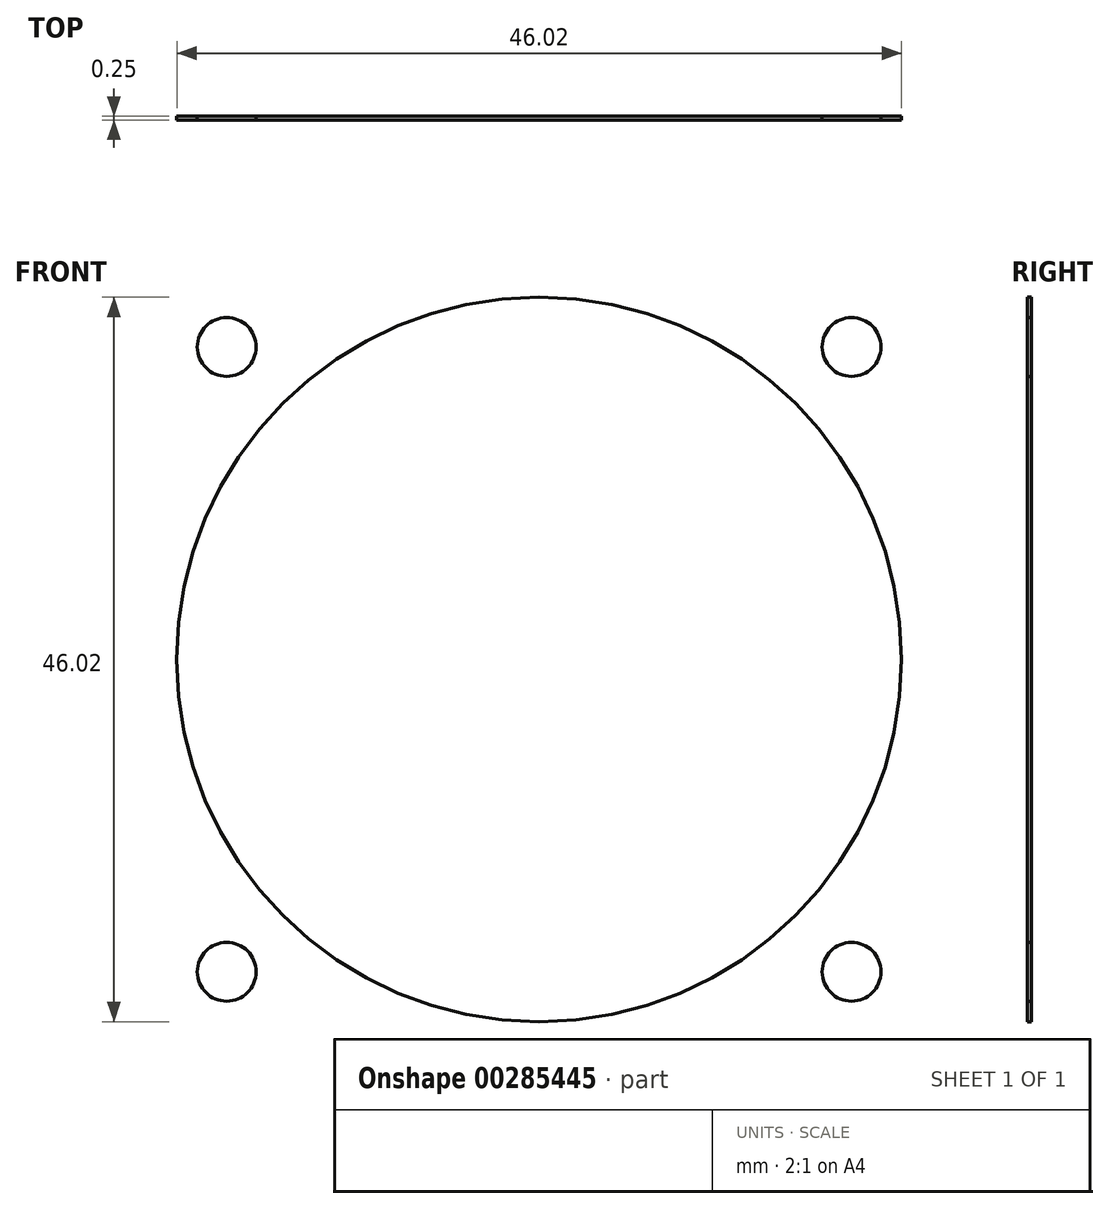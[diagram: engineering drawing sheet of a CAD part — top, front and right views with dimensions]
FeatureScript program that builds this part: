
annotation { "Feature Type Name" : "Feature", "Feature Type Description" : "" }
export const myFeature = defineFeature(function(context is Context, id is Id, definition is map)
    precondition{}
    {
        {
            var Q0;
            Q0=qCreatedBy(makeId("Front.planeOp"),FACE);
            var sketch = newSketch(context, id + "F0", { "sketchPlane" : qUnion([Q0])});
            skCircle(sketch, "E0", {"center": v(0, 0) * mm, "radius": 23.01 * mm});
            skCircle(sketch, "E1", {"center": v(-19.84, 19.84) * mm, "radius": 1.87 * mm});
            skLineSegment(sketch, "E2.bottom", {"start": v(-19.84, 19.84) * mm, "end": v(19.84, 19.84) * mm, "construction": true});
            skLineSegment(sketch, "E2.top", {"start": v(-19.84, -19.84) * mm, "end": v(19.84, -19.84) * mm, "construction": true});
            skLineSegment(sketch, "E2.left", {"start": v(-19.84, 19.84) * mm, "end": v(-19.84, -19.84) * mm, "construction": true});
            skLineSegment(sketch, "E2.right", {"start": v(19.84, 19.84) * mm, "end": v(19.84, -19.84) * mm, "construction": true});
            skLineSegment(sketch, "E3", {"start": v(0, 19.84) * mm, "end": v(0, -19.84) * mm, "construction": true});
            skLineSegment(sketch, "E4", {"start": v(-19.84, 0) * mm, "end": v(19.84, 0) * mm, "construction": true});
            skCircle(sketch, "E5", {"center": v(19.84, 19.84) * mm, "radius": 1.87 * mm});
            skCircle(sketch, "E6", {"center": v(19.84, -19.84) * mm, "radius": 1.87 * mm});
            skCircle(sketch, "E7", {"center": v(-19.84, -19.84) * mm, "radius": 1.87 * mm});
            skSolve(sketch);
        }
        {
            var Q0;
            Q0=makeQuery(id+"F0.imprint","IMPRINT",FACE,{"disambiguationData":[TD([[makeQuery(id+"F0.imprint","IMPRINT",EDGE,{"derivedFrom":sQuery(id+"F0.wireOp",EDGE,"E0")}),1.0]])]});
            var Q1;
            Q1=makeQuery(id+"F0.imprint","IMPRINT",FACE,{"disambiguationData":[TD([[makeQuery(id+"F0.imprint","IMPRINT",EDGE,{"derivedFrom":sQuery(id+"F0.wireOp",EDGE,"E1")}),1.0]])]});
            var Q2;
            Q2=makeQuery(id+"F0.imprint","IMPRINT",FACE,{"disambiguationData":[TD([[makeQuery(id+"F0.imprint","IMPRINT",EDGE,{"derivedFrom":sQuery(id+"F0.wireOp",EDGE,"E5")}),1.0]])]});
            var Q3;
            Q3=makeQuery(id+"F0.imprint","IMPRINT",FACE,{"disambiguationData":[TD([[makeQuery(id+"F0.imprint","IMPRINT",EDGE,{"derivedFrom":sQuery(id+"F0.wireOp",EDGE,"E6")}),1.0]])]});
            var Q4;
            Q4=makeQuery(id+"F0.imprint","IMPRINT",FACE,{"disambiguationData":[TD([[makeQuery(id+"F0.imprint","IMPRINT",EDGE,{"derivedFrom":sQuery(id+"F0.wireOp",EDGE,"E7")}),1.0]])]});
            extrude(context, id + "F1", {"entities" : qUnion([Q0, Q1, Q2, Q3, Q4]), "depth" : 0.25 * mm});
        }
    });
